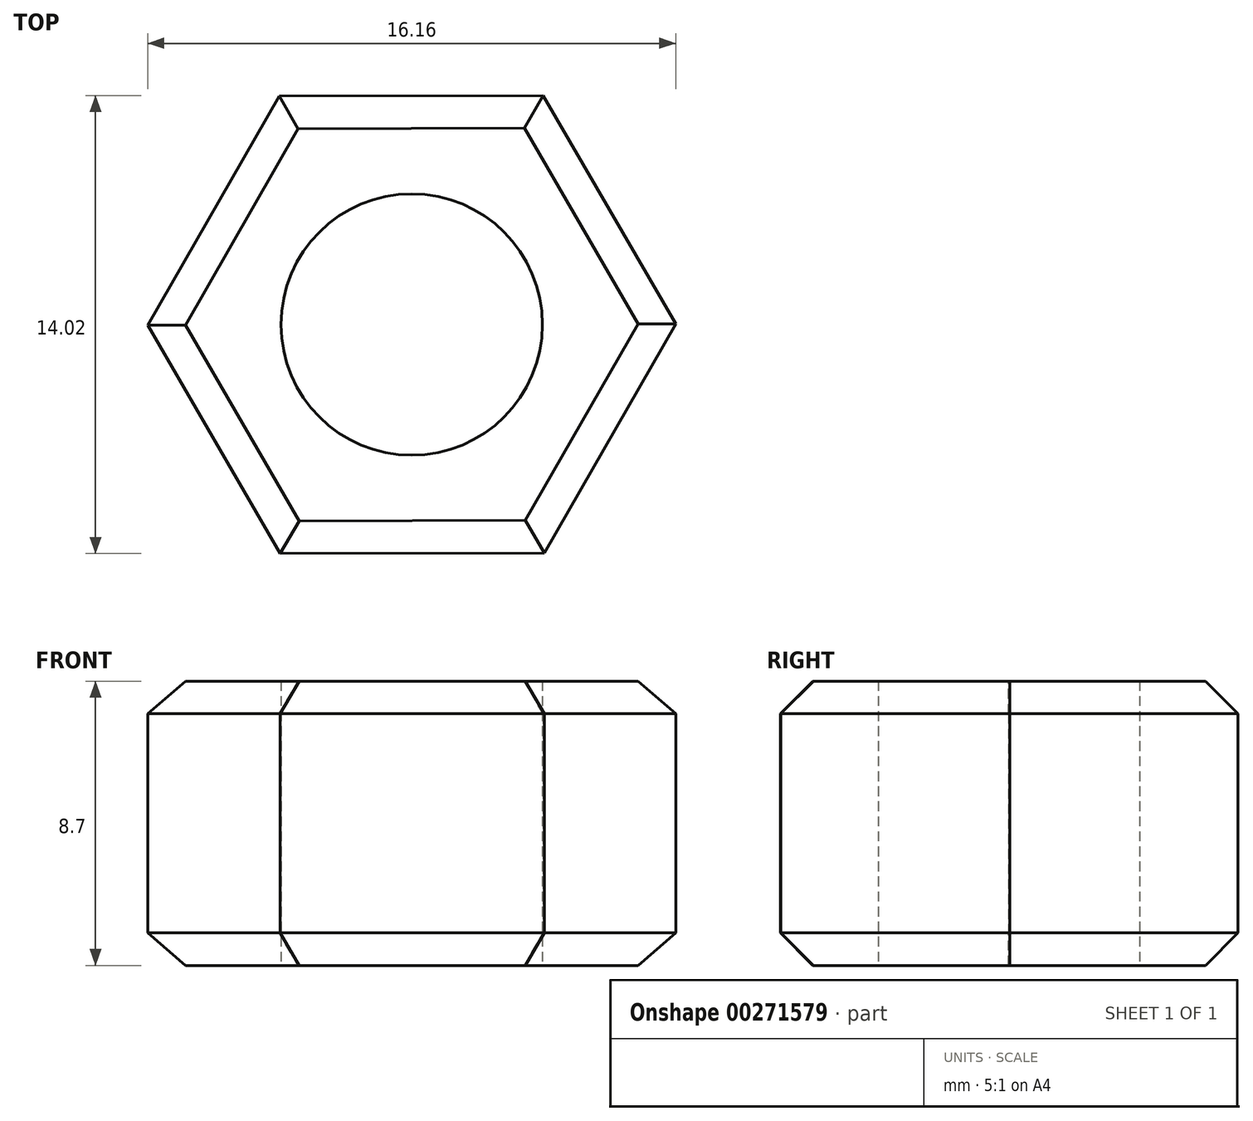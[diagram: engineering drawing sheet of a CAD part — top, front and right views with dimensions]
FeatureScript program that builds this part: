
annotation { "Feature Type Name" : "Feature", "Feature Type Description" : "" }
export const myFeature = defineFeature(function(context is Context, id is Id, definition is map)
    precondition{}
    {
        {
            var Q0;
            Q0=qCreatedBy(makeId("Top.planeOp"),FACE);
            var sketch = newSketch(context, id + "F0", { "sketchPlane" : qUnion([Q0])});
            skCircle(sketch, "E0.cCircle", {"center": v(0, 0) * mm, "radius": 7 * mm, "construction": true});
            skLineSegment(sketch, "E0.0", {"start": v(8.08, 0.02) * mm, "end": v(4.06, -7) * mm});
            skLineSegment(sketch, "E0.1", {"start": v(4.06, -7) * mm, "end": v(-4.03, -7) * mm});
            skLineSegment(sketch, "E0.2", {"start": v(-4.03, -7) * mm, "end": v(-8.08, -0.02) * mm});
            skLineSegment(sketch, "E0.3", {"start": v(-8.08, -0.02) * mm, "end": v(-4.06, 7) * mm});
            skLineSegment(sketch, "E0.4", {"start": v(-4.06, 7) * mm, "end": v(4.03, 7) * mm});
            skLineSegment(sketch, "E0.5", {"start": v(4.03, 7) * mm, "end": v(8.08, 0.02) * mm});
            skPoint(sketch, "E0.0.midPoint", {"position": v(6.07, -3.49) * mm});
            skCircle(sketch, "E1", {"center": v(0, 0) * mm, "radius": 4 * mm});
            skSolve(sketch);
        }
        {
            var Q0;
            Q0 = qSketchRegion(id + "F0", true);
            extrude(context, id + "F1", {"entities" : qUnion([Q0]), "depth" : 8.7 * mm});
        }
        {
            var Q0;
            Q0=makeQuery(id+"F1.opExtrude","CAP_EDGE",EDGE,{"disambiguationData":[OSD([sQuery(id+"F0.wireOp",EDGE,"E0.3")])],"isStart":false});
            var Q1;
            Q1=makeQuery(id+"F1.opExtrude","CAP_EDGE",EDGE,{"disambiguationData":[OSD([sQuery(id+"F0.wireOp",EDGE,"E0.2")])],"isStart":false});
            var Q2;
            Q2=makeQuery(id+"F1.opExtrude","CAP_EDGE",EDGE,{"disambiguationData":[OSD([sQuery(id+"F0.wireOp",EDGE,"E0.1")])],"isStart":false});
            var Q3;
            Q3=makeQuery(id+"F1.opExtrude","CAP_EDGE",EDGE,{"disambiguationData":[OSD([sQuery(id+"F0.wireOp",EDGE,"E0.0")])],"isStart":false});
            var Q4;
            Q4=makeQuery(id+"F1.opExtrude","CAP_EDGE",EDGE,{"disambiguationData":[OSD([sQuery(id+"F0.wireOp",EDGE,"E0.5")])],"isStart":false});
            var Q5;
            Q5=makeQuery(id+"F1.opExtrude","CAP_EDGE",EDGE,{"disambiguationData":[OSD([sQuery(id+"F0.wireOp",EDGE,"E0.4")])],"isStart":false});
            var Q6;
            Q6=makeQuery(id+"F1.opExtrude","CAP_EDGE",EDGE,{"disambiguationData":[OSD([sQuery(id+"F0.wireOp",EDGE,"E0.3")])],"isStart":true});
            var Q7;
            Q7=makeQuery(id+"F1.opExtrude","CAP_EDGE",EDGE,{"disambiguationData":[OSD([sQuery(id+"F0.wireOp",EDGE,"E0.4")])],"isStart":true});
            var Q8;
            Q8=makeQuery(id+"F1.opExtrude","CAP_EDGE",EDGE,{"disambiguationData":[OSD([sQuery(id+"F0.wireOp",EDGE,"E0.2")])],"isStart":true});
            var Q9;
            Q9=makeQuery(id+"F1.opExtrude","CAP_EDGE",EDGE,{"disambiguationData":[OSD([sQuery(id+"F0.wireOp",EDGE,"E0.1")])],"isStart":true});
            var Q10;
            Q10=makeQuery(id+"F1.opExtrude","CAP_EDGE",EDGE,{"disambiguationData":[OSD([sQuery(id+"F0.wireOp",EDGE,"E0.0")])],"isStart":true});
            var Q11;
            Q11=makeQuery(id+"F1.opExtrude","CAP_EDGE",EDGE,{"disambiguationData":[OSD([sQuery(id+"F0.wireOp",EDGE,"E0.5")])],"isStart":true});
            chamfer(context, id + "F2", {"entities" : qUnion([Q0, Q1, Q2, Q3, Q4, Q5, Q6, Q7, Q8, Q9, Q10, Q11]), "width" : 1 * mm, "tangentPropagation" : true});
        }
    });
